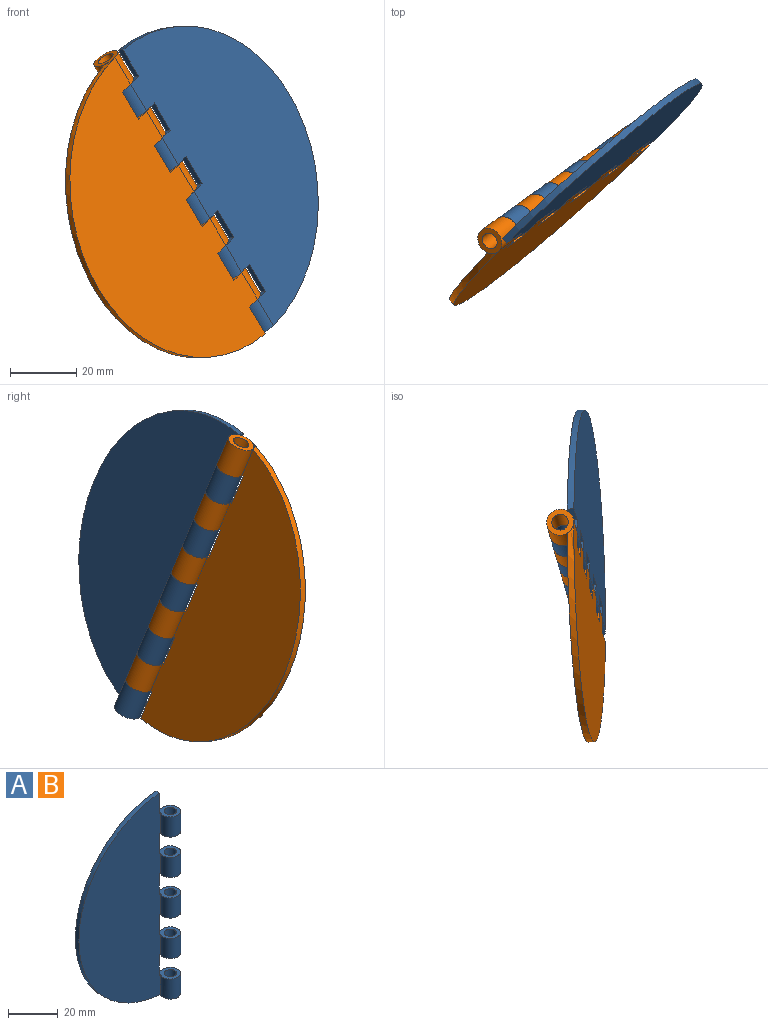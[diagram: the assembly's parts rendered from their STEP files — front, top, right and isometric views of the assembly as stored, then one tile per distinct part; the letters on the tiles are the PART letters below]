
ASSEMBLY  parts=2 mates=1
PART A: 28 faces, bbox 54.1x8.2x99.8 mm
  f0: cylinder r=2.5mm len=9.9mm, axis (0,0,-1), area 155.5mm2, adj f1,f14
  f1: plane 8.25x8.25mm, normal (0,0,-1), area 33.8mm2, adj f0,f5
  f2: cylinder r=50mm len=99.83mm, axis (0,1,0), area 300.9mm2, adj f3,f4,f5,f11
  f3: plane 99.7x46.46mm, normal (0,-1,0), area 3544.1mm2, adj f2,f5,f6,f7,f8,f9,f10,f11
  f4: plane 99.83x50mm, normal (0,1,0), area 3718.9mm2, adj f2,f5,f6,f7,f8,f9,f10,f11
  f5: cylinder r=4.12mm len=9.9mm, axis (0,0,-1), area 214.8mm2, adj f1,f2,f3,f4,f14
  f6: cylinder r=4.12mm len=9.9mm, axis (0,0,-1), area 214.5mm2, adj f3,f4,f12,f17
  f7: cylinder r=4.12mm len=9.9mm, axis (0,0,-1), area 214.5mm2, adj f3,f4,f15,f20
  f8: cylinder r=4.12mm len=9.9mm, axis (0,0,-1), area 214.5mm2, adj f3,f4,f18,f23
  f9: cylinder r=4.12mm len=9.9mm, axis (0,0,-1), area 214.5mm2, adj f3,f4,f10,f21
  f10: plane 8.25x8.25mm, normal (0,0,1), area 37.1mm2, adj f3,f4,f9,f11,f27
  f11: plane 9.93x2mm, normal (1,0,0), area 19.9mm2, adj f2,f3,f4,f10
  f12: plane 8.25x8.25mm, normal (0,0,-1), area 37.1mm2, adj f3,f4,f6,f13,f24
  f13: plane 10.1x2mm, normal (1,0,0), area 20.2mm2, adj f3,f4,f12,f14
  f14: plane 8.25x8.25mm, normal (0,0,1), area 37.1mm2, adj f0,f3,f4,f5,f13
  f15: plane 8.25x8.25mm, normal (0,0,-1), area 37.1mm2, adj f3,f4,f7,f16,f25
  f16: plane 10.1x2mm, normal (1,0,0), area 20.2mm2, adj f3,f4,f15,f17
  f17: plane 8.25x8.25mm, normal (0,0,1), area 37.1mm2, adj f3,f4,f6,f16,f24
  f18: plane 8.25x8.25mm, normal (0,0,-1), area 37.1mm2, adj f3,f4,f8,f19,f26
  f19: plane 10.1x2mm, normal (1,0,0), area 20.2mm2, adj f3,f4,f18,f20
  f20: plane 8.25x8.25mm, normal (0,0,1), area 37.1mm2, adj f3,f4,f7,f19,f25
  f21: plane 8.25x8.25mm, normal (0,0,-1), area 37.1mm2, adj f3,f4,f9,f22,f27
  f22: plane 10.1x2mm, normal (1,0,0), area 20.2mm2, adj f3,f4,f21,f23
  f23: plane 8.25x8.25mm, normal (0,0,1), area 37.1mm2, adj f3,f4,f8,f22,f26
  f24: cylinder r=2.5mm len=9.9mm, axis (0,0,-1), area 155.5mm2, adj f12,f17
  f25: cylinder r=2.5mm len=9.9mm, axis (0,0,-1), area 155.5mm2, adj f15,f20
  f26: cylinder r=2.5mm len=9.9mm, axis (0,0,-1), area 155.5mm2, adj f18,f23
  f27: cylinder r=2.5mm len=9.9mm, axis (0,0,-1), area 155.5mm2, adj f10,f21
PART B: same geometry as A
PLACE A rot(axis=(0.32,0.08,-0.94),139.1deg) t=(-4.4,-17.31,36.68)mm
PLACE B rot(axis=(-0.89,-0.35,-0.3),171.4deg) t=(-4.35,-17.28,36.6)mm
MATE revolute A.f0 <-> B.f0  axis (0.48,0.34,-0.81) through (-25.52,-28.66,68.73)mm
